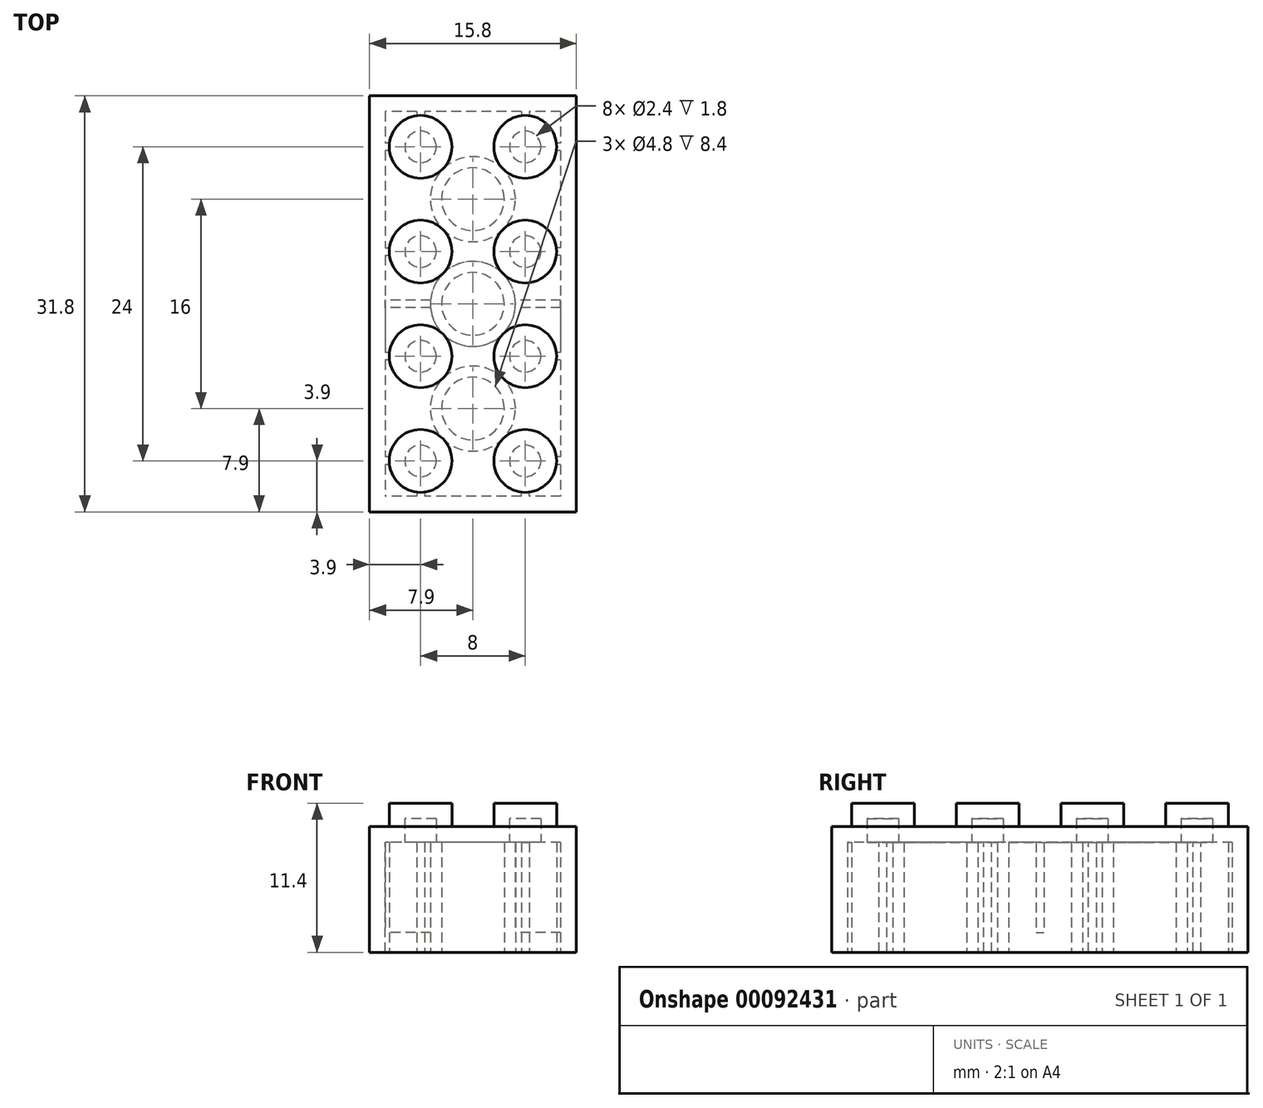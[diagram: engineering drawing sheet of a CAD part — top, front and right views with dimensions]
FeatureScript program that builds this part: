
annotation { "Feature Type Name" : "Feature", "Feature Type Description" : "" }
export const myFeature = defineFeature(function(context is Context, id is Id, definition is map)
    precondition{}
    {
        {
            var Q0;
            Q0=qCreatedBy(makeId("Top.planeOp"),FACE);
            var sketch = newSketch(context, id + "F0", { "sketchPlane" : qUnion([Q0])});
            skLineSegment(sketch, "E0.bottom", {"start": v(7.9, 15.9) * mm, "end": v(-7.9, 15.9) * mm});
            skLineSegment(sketch, "E0.top", {"start": v(7.9, -15.9) * mm, "end": v(-7.9, -15.9) * mm});
            skLineSegment(sketch, "E0.left", {"start": v(7.9, 15.9) * mm, "end": v(7.9, -15.9) * mm});
            skLineSegment(sketch, "E0.right", {"start": v(-7.9, 15.9) * mm, "end": v(-7.9, -15.9) * mm});
            skPoint(sketch, "E0.middle", {"position": v(0, 0) * mm});
            skCircle(sketch, "E1", {"center": v(4, 4) * mm, "radius": 2.4 * mm});
            skCircle(sketch, "E2", {"center": v(-4, 4) * mm, "radius": 2.4 * mm});
            skCircle(sketch, "E3", {"center": v(-4, -4) * mm, "radius": 2.4 * mm});
            skCircle(sketch, "E4", {"center": v(4, -4) * mm, "radius": 2.4 * mm});
            skCircle(sketch, "E5", {"center": v(4, -12) * mm, "radius": 2.4 * mm});
            skCircle(sketch, "E6", {"center": v(-4, -12) * mm, "radius": 2.4 * mm});
            skCircle(sketch, "E7", {"center": v(-4, 12) * mm, "radius": 2.4 * mm});
            skCircle(sketch, "E8", {"center": v(4, 12) * mm, "radius": 2.4 * mm});
            skSolve(sketch);
        }
        {
            var Q0;
            Q0=makeQuery(id+"F0.imprint","IMPRINT",FACE,{"disambiguationData":[TD([[makeQuery(id+"F0.imprint","IMPRINT",EDGE,{"derivedFrom":sQuery(id+"F0.wireOp",EDGE,"E1")}),1.0]])]});
            var Q1;
            Q1=makeQuery(id+"F0.imprint","IMPRINT",FACE,{"disambiguationData":[TD([[makeQuery(id+"F0.imprint","IMPRINT",EDGE,{"derivedFrom":sQuery(id+"F0.wireOp",EDGE,"E8")}),1.0]])]});
            var Q2;
            Q2=makeQuery(id+"F0.imprint","IMPRINT",FACE,{"disambiguationData":[TD([[makeQuery(id+"F0.imprint","IMPRINT",EDGE,{"derivedFrom":sQuery(id+"F0.wireOp",EDGE,"E4")}),1.0]])]});
            var Q3;
            Q3=makeQuery(id+"F0.imprint","IMPRINT",FACE,{"disambiguationData":[TD([[makeQuery(id+"F0.imprint","IMPRINT",EDGE,{"derivedFrom":sQuery(id+"F0.wireOp",EDGE,"E5")}),1.0]])]});
            var Q4;
            Q4=makeQuery(id+"F0.imprint","IMPRINT",FACE,{"disambiguationData":[TD([[makeQuery(id+"F0.imprint","IMPRINT",EDGE,{"derivedFrom":sQuery(id+"F0.wireOp",EDGE,"E6")}),1.0]])]});
            var Q5;
            Q5=makeQuery(id+"F0.imprint","IMPRINT",FACE,{"disambiguationData":[TD([[makeQuery(id+"F0.imprint","IMPRINT",EDGE,{"derivedFrom":sQuery(id+"F0.wireOp",EDGE,"E3")}),1.0]])]});
            var Q6;
            Q6=makeQuery(id+"F0.imprint","IMPRINT",FACE,{"disambiguationData":[TD([[makeQuery(id+"F0.imprint","IMPRINT",EDGE,{"derivedFrom":sQuery(id+"F0.wireOp",EDGE,"E2")}),1.0]])]});
            var Q7;
            Q7=makeQuery(id+"F0.imprint","IMPRINT",FACE,{"disambiguationData":[TD([[makeQuery(id+"F0.imprint","IMPRINT",EDGE,{"derivedFrom":sQuery(id+"F0.wireOp",EDGE,"E7")}),1.0]])]});
            var Q8;
            Q8=makeQuery(id+"F0.imprint","IMPRINT",FACE,{"disambiguationData":[TD([[makeQuery(id+"F0.imprint","IMPRINT",EDGE,{"derivedFrom":sQuery(id+"F0.wireOp",EDGE,"E0.bottom")}),1.0]])]});
            extrude(context, id + "F1", {"entities" : qUnion([Q0, Q1, Q2, Q3, Q4, Q5, Q6, Q7, Q8]), "depth" : 9.6 * mm});
        }
        {
            var Q0;
            Q0=makeQuery(id+"F0.imprint","IMPRINT",FACE,{"disambiguationData":[TD([[makeQuery(id+"F0.imprint","IMPRINT",EDGE,{"derivedFrom":sQuery(id+"F0.wireOp",EDGE,"E7")}),1.0]])]});
            var Q1;
            Q1=makeQuery(id+"F0.imprint","IMPRINT",FACE,{"disambiguationData":[TD([[makeQuery(id+"F0.imprint","IMPRINT",EDGE,{"derivedFrom":sQuery(id+"F0.wireOp",EDGE,"E8")}),1.0]])]});
            var Q2;
            Q2=makeQuery(id+"F0.imprint","IMPRINT",FACE,{"disambiguationData":[TD([[makeQuery(id+"F0.imprint","IMPRINT",EDGE,{"derivedFrom":sQuery(id+"F0.wireOp",EDGE,"E1")}),1.0]])]});
            var Q3;
            Q3=makeQuery(id+"F0.imprint","IMPRINT",FACE,{"disambiguationData":[TD([[makeQuery(id+"F0.imprint","IMPRINT",EDGE,{"derivedFrom":sQuery(id+"F0.wireOp",EDGE,"E4")}),1.0]])]});
            var Q4;
            Q4=makeQuery(id+"F0.imprint","IMPRINT",FACE,{"disambiguationData":[TD([[makeQuery(id+"F0.imprint","IMPRINT",EDGE,{"derivedFrom":sQuery(id+"F0.wireOp",EDGE,"E3")}),1.0]])]});
            var Q5;
            Q5=makeQuery(id+"F0.imprint","IMPRINT",FACE,{"disambiguationData":[TD([[makeQuery(id+"F0.imprint","IMPRINT",EDGE,{"derivedFrom":sQuery(id+"F0.wireOp",EDGE,"E2")}),1.0]])]});
            var Q6;
            Q6=makeQuery(id+"F0.imprint","IMPRINT",FACE,{"disambiguationData":[TD([[makeQuery(id+"F0.imprint","IMPRINT",EDGE,{"derivedFrom":sQuery(id+"F0.wireOp",EDGE,"E6")}),1.0]])]});
            var Q7;
            Q7=makeQuery(id+"F0.imprint","IMPRINT",FACE,{"disambiguationData":[TD([[makeQuery(id+"F0.imprint","IMPRINT",EDGE,{"derivedFrom":sQuery(id+"F0.wireOp",EDGE,"E5")}),1.0]])]});
            extrude(context, id + "F2", {"entities" : qUnion([Q0, Q1, Q2, Q3, Q4, Q5, Q6, Q7]), "operationType" : NewBodyOperationType.ADD, "depth" : 11.4 * mm});
        }
        {
            var Q0;
            Q0=makeQuery(id+"F1.opExtrude","CAP_FACE",FACE,{"disambiguationData":[OSD([sQuery(id+"F0.wireOp",EDGE,"E0.bottom"),sQuery(id+"F0.wireOp",EDGE,"E0.top"),sQuery(id+"F0.wireOp",EDGE,"E0.left"),sQuery(id+"F0.wireOp",EDGE,"E0.right")])],"isStart":true});
            shell(context, id + "F3", {"entities" : qUnion([Q0]), "thickness" : 1.2 * mm});
        }
        {
            var Q0;
            Q0=qCreatedBy(makeId("Top.planeOp"),FACE);
            var sketch = newSketch(context, id + "F4", { "sketchPlane" : qUnion([Q0])});
            skCircle(sketch, "E9", {"center": v(0, 0) * mm, "radius": 3.25 * mm});
            skCircle(sketch, "E10", {"center": v(0, 0) * mm, "radius": 2.4 * mm});
            skCircle(sketch, "E11", {"center": v(0, -8) * mm, "radius": 3.25 * mm});
            skCircle(sketch, "E12", {"center": v(0, 8) * mm, "radius": 3.25 * mm});
            skCircle(sketch, "E13", {"center": v(0, -8) * mm, "radius": 2.4 * mm});
            skCircle(sketch, "E14", {"center": v(0, 8) * mm, "radius": 2.4 * mm});
            skLineSegment(sketch, "E15.bottom", {"start": v(6.7, -0.3) * mm, "end": v(3.24, -0.3) * mm});
            skLineSegment(sketch, "E15.top", {"start": v(6.7, 0.3) * mm, "end": v(3.24, 0.3) * mm});
            skLineSegment(sketch, "E15.left", {"start": v(6.7, -0.3) * mm, "end": v(6.7, 0.3) * mm});
            skLineSegment(sketch, "E15.right", {"start": v(-6.7, -0.3) * mm, "end": v(-6.7, 0.3) * mm});
            skLineSegment(sketch, "E16.trimOffspring", {"start": v(-3.24, 0.3) * mm, "end": v(-6.7, 0.3) * mm});
            skLineSegment(sketch, "E17.trimOffspring", {"start": v(-3.24, -0.3) * mm, "end": v(-6.7, -0.3) * mm});
            skSolve(sketch);
        }
        {
            var Q0;
            Q0=qCreatedBy(makeId("Top.planeOp"),FACE);
            var sketch = newSketch(context, id + "F5", { "sketchPlane" : qUnion([Q0])});
            skPoint(sketch, "E18.middle", {"position": v(0, 0) * mm});
            skLineSegment(sketch, "E19.bottom", {"start": v(-3.7, -14.4) * mm, "end": v(-4.3, -14.4) * mm});
            skLineSegment(sketch, "E19.top", {"start": v(-3.7, -15) * mm, "end": v(-4.3, -15) * mm});
            skLineSegment(sketch, "E19.left", {"start": v(-3.7, -14.4) * mm, "end": v(-3.7, -15) * mm});
            skLineSegment(sketch, "E19.right", {"start": v(-4.3, -14.4) * mm, "end": v(-4.3, -15) * mm});
            skPoint(sketch, "E19.middle", {"position": v(-4, -14.7) * mm});
            skLineSegment(sketch, "E20.bottom", {"start": v(3.7, -15) * mm, "end": v(4.3, -15) * mm});
            skLineSegment(sketch, "E20.top", {"start": v(3.7, -14.4) * mm, "end": v(4.3, -14.4) * mm});
            skLineSegment(sketch, "E20.left", {"start": v(3.7, -15) * mm, "end": v(3.7, -14.4) * mm});
            skLineSegment(sketch, "E20.right", {"start": v(4.3, -15) * mm, "end": v(4.3, -14.4) * mm});
            skPoint(sketch, "E20.middle", {"position": v(4, -14.7) * mm});
            skLineSegment(sketch, "E21.bottom", {"start": v(6.4, -12.3) * mm, "end": v(7, -12.3) * mm});
            skLineSegment(sketch, "E21.top", {"start": v(6.4, -11.7) * mm, "end": v(7, -11.7) * mm});
            skLineSegment(sketch, "E21.left", {"start": v(6.4, -12.3) * mm, "end": v(6.4, -11.7) * mm});
            skLineSegment(sketch, "E21.right", {"start": v(7, -12.3) * mm, "end": v(7, -11.7) * mm});
            skPoint(sketch, "E21.middle", {"position": v(6.7, -12) * mm});
            skLineSegment(sketch, "E22.bottom", {"start": v(-6.4, -12.3) * mm, "end": v(-7, -12.3) * mm});
            skLineSegment(sketch, "E22.top", {"start": v(-6.4, -11.7) * mm, "end": v(-7, -11.7) * mm});
            skLineSegment(sketch, "E22.left", {"start": v(-6.4, -12.3) * mm, "end": v(-6.4, -11.7) * mm});
            skLineSegment(sketch, "E22.right", {"start": v(-7, -12.3) * mm, "end": v(-7, -11.7) * mm});
            skPoint(sketch, "E22.middle", {"position": v(-6.7, -12) * mm});
            skLineSegment(sketch, "E23.bottom", {"start": v(-6.4, -4.3) * mm, "end": v(-7, -4.3) * mm});
            skLineSegment(sketch, "E23.top", {"start": v(-6.4, -3.7) * mm, "end": v(-7, -3.7) * mm});
            skLineSegment(sketch, "E23.left", {"start": v(-6.4, -4.3) * mm, "end": v(-6.4, -3.7) * mm});
            skLineSegment(sketch, "E23.right", {"start": v(-7, -4.3) * mm, "end": v(-7, -3.7) * mm});
            skPoint(sketch, "E23.middle", {"position": v(-6.7, -4) * mm});
            skLineSegment(sketch, "E24.bottom", {"start": v(6.4, -4.3) * mm, "end": v(7, -4.3) * mm});
            skLineSegment(sketch, "E24.top", {"start": v(6.4, -3.7) * mm, "end": v(7, -3.7) * mm});
            skLineSegment(sketch, "E24.left", {"start": v(6.4, -4.3) * mm, "end": v(6.4, -3.7) * mm});
            skLineSegment(sketch, "E24.right", {"start": v(7, -4.3) * mm, "end": v(7, -3.7) * mm});
            skPoint(sketch, "E24.middle", {"position": v(6.7, -4) * mm});
            skLineSegment(sketch, "E25.bottom", {"start": v(-7, 3.7) * mm, "end": v(-6.4, 3.7) * mm});
            skLineSegment(sketch, "E25.top", {"start": v(-7, 4.3) * mm, "end": v(-6.4, 4.3) * mm});
            skLineSegment(sketch, "E25.left", {"start": v(-7, 3.7) * mm, "end": v(-7, 4.3) * mm});
            skLineSegment(sketch, "E25.right", {"start": v(-6.4, 3.7) * mm, "end": v(-6.4, 4.3) * mm});
            skPoint(sketch, "E25.middle", {"position": v(-6.7, 4) * mm});
            skLineSegment(sketch, "E26.bottom", {"start": v(6.4, 3.7) * mm, "end": v(7, 3.7) * mm});
            skLineSegment(sketch, "E26.top", {"start": v(6.4, 4.3) * mm, "end": v(7, 4.3) * mm});
            skLineSegment(sketch, "E26.left", {"start": v(6.4, 3.7) * mm, "end": v(6.4, 4.3) * mm});
            skLineSegment(sketch, "E26.right", {"start": v(7, 3.7) * mm, "end": v(7, 4.3) * mm});
            skPoint(sketch, "E26.middle", {"position": v(6.7, 4) * mm});
            skLineSegment(sketch, "E27.bottom", {"start": v(6.4, 11.7) * mm, "end": v(7, 11.7) * mm});
            skLineSegment(sketch, "E27.top", {"start": v(6.4, 12.3) * mm, "end": v(7, 12.3) * mm});
            skLineSegment(sketch, "E27.left", {"start": v(6.4, 11.7) * mm, "end": v(6.4, 12.3) * mm});
            skLineSegment(sketch, "E27.right", {"start": v(7, 11.7) * mm, "end": v(7, 12.3) * mm});
            skPoint(sketch, "E27.middle", {"position": v(6.7, 12) * mm});
            skLineSegment(sketch, "E28.bottom", {"start": v(-6.4, 11.7) * mm, "end": v(-7, 11.7) * mm});
            skLineSegment(sketch, "E28.top", {"start": v(-6.4, 12.3) * mm, "end": v(-7, 12.3) * mm});
            skLineSegment(sketch, "E28.left", {"start": v(-6.4, 11.7) * mm, "end": v(-6.4, 12.3) * mm});
            skLineSegment(sketch, "E28.right", {"start": v(-7, 11.7) * mm, "end": v(-7, 12.3) * mm});
            skPoint(sketch, "E28.middle", {"position": v(-6.7, 12) * mm});
            skLineSegment(sketch, "E29.bottom", {"start": v(-3.7, 14.4) * mm, "end": v(-4.3, 14.4) * mm});
            skLineSegment(sketch, "E29.top", {"start": v(-3.7, 15) * mm, "end": v(-4.3, 15) * mm});
            skLineSegment(sketch, "E29.left", {"start": v(-3.7, 14.4) * mm, "end": v(-3.7, 15) * mm});
            skLineSegment(sketch, "E29.right", {"start": v(-4.3, 14.4) * mm, "end": v(-4.3, 15) * mm});
            skPoint(sketch, "E29.middle", {"position": v(-4, 14.7) * mm});
            skLineSegment(sketch, "E30.bottom", {"start": v(3.7, 14.4) * mm, "end": v(4.3, 14.4) * mm});
            skLineSegment(sketch, "E30.top", {"start": v(3.7, 15) * mm, "end": v(4.3, 15) * mm});
            skLineSegment(sketch, "E30.left", {"start": v(3.7, 14.4) * mm, "end": v(3.7, 15) * mm});
            skLineSegment(sketch, "E30.right", {"start": v(4.3, 14.4) * mm, "end": v(4.3, 15) * mm});
            skPoint(sketch, "E30.middle", {"position": v(4, 14.7) * mm});
            skSolve(sketch);
        }
        {
            var Q0;
            Q0 = qSketchRegion(id + "F5", true);
            extrude(context, id + "F6", {"entities" : qUnion([Q0]), "operationType" : NewBodyOperationType.ADD, "endBound" : BoundingType.UP_TO_NEXT, "depth" : 25 * mm});
        }
        {
            var Q0;
            Q0=makeQuery(id+"F4.imprint","IMPRINT",FACE,{"disambiguationData":[TD([[makeQuery(id+"F4.imprint","IMPRINT",EDGE,{"derivedFrom":sQuery(id+"F4.wireOp",EDGE,"E11")}),1.0]])]});
            var Q1;
            Q1=makeQuery(id+"F4.imprint","IMPRINT",FACE,{"disambiguationData":[TD([[makeQuery(id+"F4.imprint","IMPRINT",EDGE,{"derivedFrom":sQuery(id+"F4.wireOp",EDGE,"E10")}),-1.0]])]});
            var Q2;
            Q2=makeQuery(id+"F4.imprint","IMPRINT",FACE,{"disambiguationData":[TD([[makeQuery(id+"F4.imprint","IMPRINT",EDGE,{"derivedFrom":sQuery(id+"F4.wireOp",EDGE,"E12")}),1.0]])]});
            extrude(context, id + "F7", {"entities" : qUnion([Q0, Q1, Q2]), "operationType" : NewBodyOperationType.ADD, "endBound" : BoundingType.UP_TO_NEXT, "depth" : 25 * mm});
        }
        {
            var Q0;
            Q0=makeQuery(id+"F4.imprint","IMPRINT",FACE,{"disambiguationData":[TD([[makeQuery(id+"F4.imprint","IMPRINT",EDGE,{"derivedFrom":sQuery(id+"F4.wireOp",EDGE,"E15.right")}),-1.0]])]});
            var Q1;
            {var subQ0=sQuery(id+"F4.wireOp",EDGE,"E15.bottom");Q1=makeQuery(id+"F4.imprint","IMPRINT",FACE,{"disambiguationData":[TD([[makeQuery(id+"F4.imprint","IMPRINT",EDGE,{"derivedFrom":subQ0}),-1.0]])]});}
            extrude(context, id + "F8", {"entities" : qUnion([Q0, Q1]), "operationType" : NewBodyOperationType.ADD, "endBound" : BoundingType.UP_TO_NEXT, "depth" : 25 * mm, "hasSecondDirection" : true, "secondDirectionOppositeDirection" : false, "secondDirectionDepth" : 1.5 * mm});
        }
    });
